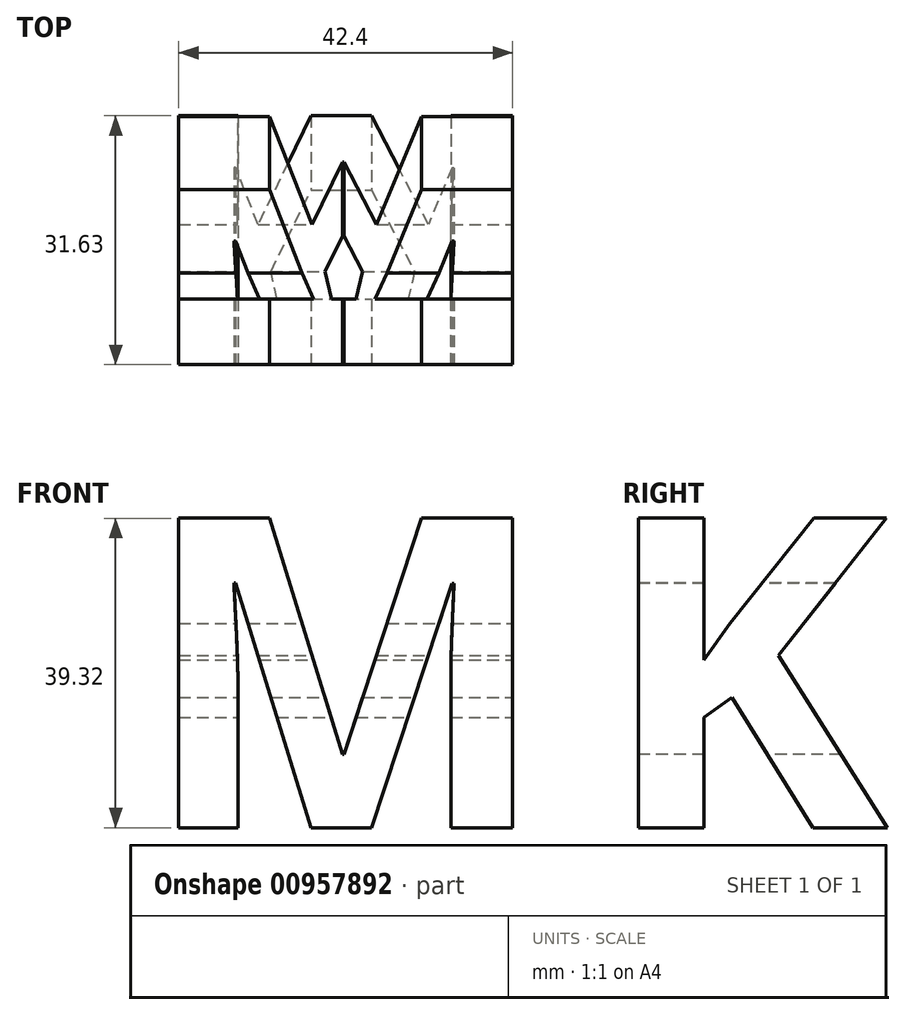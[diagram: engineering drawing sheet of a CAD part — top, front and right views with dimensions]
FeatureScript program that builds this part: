
annotation { "Feature Type Name" : "Feature", "Feature Type Description" : "" }
export const myFeature = defineFeature(function(context is Context, id is Id, definition is map)
    precondition{}
    {
        {
            var Q0;
            Q0=qCreatedBy(makeId("Front.planeOp"),FACE);
            var sketch = newSketch(context, id + "F0", { "sketchPlane" : qUnion([Q0])});
            skText(sketch, "E0", { "text": "M", "fontName": "OpenSans-Bold.ttf"});
            const initialGuessF0  = {"E0": [0, 0, 1, 0, 0.04]};
            skSetInitialGuess(sketch, initialGuessF0);
            skSolve(sketch);
        }
        {
            var Q0;
            Q0=makeQuery(id+"F0.imprint","IMPRINT",FACE,{"disambiguationData":[TD([[makeQuery(id+"F0.imprint","IMPRINT",EDGE,{"derivedFrom":sQuery(id+"F0.wireOp",EDGE,"E0.sketch_text.stroke-0")}),-1.0]])]});
            extrude(context, id + "F1", {"entities" : qUnion([Q0]), "flatOperationType" : FlatOperationType.REMOVE, "oppositeDirection" : true, "depth" : 40 * mm, "offsetDistance" : 25 * mm, "domain" : OperationDomain.MODEL});
        }
        {
            var Q0;
            Q0=makeQuery(id+"F1.opExtrude","SWEPT_FACE",FACE,{"disambiguationData":[OSD([sQuery(id+"F0.wireOp",EDGE,"E0.sketch_text.stroke-11")])]});
            var sketch = newSketch(context, id + "F2", { "sketchPlane" : qUnion([Q0])});
            skText(sketch, "E1", { "text": "K", "fontName": "OpenSans-Bold.ttf"});
            const initialGuessF2  = {"E1": [0, 0, 1, 0, 0.03966]};
            skSetInitialGuess(sketch, initialGuessF2);
            skSolve(sketch);
        }
        {
            var Q0;
            Q0 = qSketchRegion(id + "F2", true);
            var Q1;
            Q1=makeQuery(id+"F1.opExtrude","SWEPT_FACE",FACE,{"disambiguationData":[OSD([sQuery(id+"F0.wireOp",EDGE,"E0.sketch_text.stroke-5")])]});
            extrude(context, id + "F3", {"entities" : qUnion([Q0]), "endBound" : BoundingType.UP_TO_SURFACE, "oppositeDirection" : true, "depth" : 26.3 * mm, "endBoundEntityFace" : qUnion([Q1]), "offsetDistance" : 25 * mm});
        }
        {
            var Q0;
            Q0=makeQuery(id+"F3.opExtrude","SWEPT_BODY",BODY,{"disambiguationData":[OSD([sQuery(id+"F2.wireOp",EDGE,"E1.sketch_text.stroke-0"),sQuery(id+"F2.wireOp",EDGE,"E1.sketch_text.stroke-1"),sQuery(id+"F2.wireOp",EDGE,"E1.sketch_text.stroke-2"),sQuery(id+"F2.wireOp",EDGE,"E1.sketch_text.stroke-3"),sQuery(id+"F2.wireOp",EDGE,"E1.sketch_text.stroke-4"),sQuery(id+"F2.wireOp",EDGE,"E1.sketch_text.stroke-5"),sQuery(id+"F2.wireOp",EDGE,"E1.sketch_text.stroke-6"),sQuery(id+"F2.wireOp",EDGE,"E1.sketch_text.stroke-7"),sQuery(id+"F2.wireOp",EDGE,"E1.sketch_text.stroke-8"),sQuery(id+"F2.wireOp",EDGE,"E1.sketch_text.stroke-9"),sQuery(id+"F2.wireOp",EDGE,"E1.sketch_text.stroke-10"),sQuery(id+"F2.wireOp",EDGE,"E1.sketch_text.stroke-11"),sQuery(id+"F2.wireOp",EDGE,"E1.sketch_text.stroke-12")])]});
            var Q1;
            Q1=makeQuery(id+"F1.opExtrude","SWEPT_BODY",BODY,{"disambiguationData":[OSD([sQuery(id+"F0.wireOp",EDGE,"E0.sketch_text.stroke-0"),sQuery(id+"F0.wireOp",EDGE,"E0.sketch_text.stroke-1"),sQuery(id+"F0.wireOp",EDGE,"E0.sketch_text.stroke-2"),sQuery(id+"F0.wireOp",EDGE,"E0.sketch_text.stroke-3"),sQuery(id+"F0.wireOp",EDGE,"E0.sketch_text.stroke-4"),sQuery(id+"F0.wireOp",EDGE,"E0.sketch_text.stroke-5"),sQuery(id+"F0.wireOp",EDGE,"E0.sketch_text.stroke-6"),sQuery(id+"F0.wireOp",EDGE,"E0.sketch_text.stroke-7"),sQuery(id+"F0.wireOp",EDGE,"E0.sketch_text.stroke-8"),sQuery(id+"F0.wireOp",EDGE,"E0.sketch_text.stroke-9"),sQuery(id+"F0.wireOp",EDGE,"E0.sketch_text.stroke-10"),sQuery(id+"F0.wireOp",EDGE,"E0.sketch_text.stroke-11"),sQuery(id+"F0.wireOp",EDGE,"E0.sketch_text.stroke-12"),sQuery(id+"F0.wireOp",EDGE,"E0.sketch_text.stroke-13"),sQuery(id+"F0.wireOp",EDGE,"E0.sketch_text.stroke-14"),sQuery(id+"F0.wireOp",EDGE,"E0.sketch_text.stroke-15"),sQuery(id+"F0.wireOp",EDGE,"E0.sketch_text.stroke-16"),sQuery(id+"F0.wireOp",EDGE,"E0.sketch_text.stroke-17"),sQuery(id+"F0.wireOp",EDGE,"E0.sketch_text.stroke-18")])]});
            var Q2;
            Q2=makeQuery(id+"F1.opExtrude","SWEPT_BODY",BODY,{"disambiguationData":[OSD([sQuery(id+"F0.wireOp",EDGE,"E0.sketch_text.stroke-0"),sQuery(id+"F0.wireOp",EDGE,"E0.sketch_text.stroke-1"),sQuery(id+"F0.wireOp",EDGE,"E0.sketch_text.stroke-2"),sQuery(id+"F0.wireOp",EDGE,"E0.sketch_text.stroke-3"),sQuery(id+"F0.wireOp",EDGE,"E0.sketch_text.stroke-4"),sQuery(id+"F0.wireOp",EDGE,"E0.sketch_text.stroke-5"),sQuery(id+"F0.wireOp",EDGE,"E0.sketch_text.stroke-6"),sQuery(id+"F0.wireOp",EDGE,"E0.sketch_text.stroke-7"),sQuery(id+"F0.wireOp",EDGE,"E0.sketch_text.stroke-8"),sQuery(id+"F0.wireOp",EDGE,"E0.sketch_text.stroke-9"),sQuery(id+"F0.wireOp",EDGE,"E0.sketch_text.stroke-10"),sQuery(id+"F0.wireOp",EDGE,"E0.sketch_text.stroke-11"),sQuery(id+"F0.wireOp",EDGE,"E0.sketch_text.stroke-12"),sQuery(id+"F0.wireOp",EDGE,"E0.sketch_text.stroke-13"),sQuery(id+"F0.wireOp",EDGE,"E0.sketch_text.stroke-14"),sQuery(id+"F0.wireOp",EDGE,"E0.sketch_text.stroke-15"),sQuery(id+"F0.wireOp",EDGE,"E0.sketch_text.stroke-16"),sQuery(id+"F0.wireOp",EDGE,"E0.sketch_text.stroke-17"),sQuery(id+"F0.wireOp",EDGE,"E0.sketch_text.stroke-18")])]});
            booleanBodies(context, id + "F4", {"operationType" : BooleanOperationType.INTERSECTION, "tools" : qUnion([Q0, Q1]), "targets" : qUnion([Q2])});
        }
        {
            var Q0;
            Q0=makeQuery(id+"F4.opBoolean","INTERSECT",BODY,{"derivedFrom":[makeQuery(id+"F1.opExtrude","SWEPT_BODY",BODY,{"disambiguationData":[OSD([sQuery(id+"F0.wireOp",EDGE,"E0.sketch_text.stroke-0"),sQuery(id+"F0.wireOp",EDGE,"E0.sketch_text.stroke-1"),sQuery(id+"F0.wireOp",EDGE,"E0.sketch_text.stroke-2"),sQuery(id+"F0.wireOp",EDGE,"E0.sketch_text.stroke-3"),sQuery(id+"F0.wireOp",EDGE,"E0.sketch_text.stroke-4"),sQuery(id+"F0.wireOp",EDGE,"E0.sketch_text.stroke-5"),sQuery(id+"F0.wireOp",EDGE,"E0.sketch_text.stroke-6"),sQuery(id+"F0.wireOp",EDGE,"E0.sketch_text.stroke-7"),sQuery(id+"F0.wireOp",EDGE,"E0.sketch_text.stroke-8"),sQuery(id+"F0.wireOp",EDGE,"E0.sketch_text.stroke-9"),sQuery(id+"F0.wireOp",EDGE,"E0.sketch_text.stroke-10"),sQuery(id+"F0.wireOp",EDGE,"E0.sketch_text.stroke-11"),sQuery(id+"F0.wireOp",EDGE,"E0.sketch_text.stroke-12"),sQuery(id+"F0.wireOp",EDGE,"E0.sketch_text.stroke-13"),sQuery(id+"F0.wireOp",EDGE,"E0.sketch_text.stroke-14"),sQuery(id+"F0.wireOp",EDGE,"E0.sketch_text.stroke-15"),sQuery(id+"F0.wireOp",EDGE,"E0.sketch_text.stroke-16"),sQuery(id+"F0.wireOp",EDGE,"E0.sketch_text.stroke-17"),sQuery(id+"F0.wireOp",EDGE,"E0.sketch_text.stroke-18")])]}),makeQuery(id+"F3.opExtrude","SWEPT_BODY",BODY,{"disambiguationData":[OSD([sQuery(id+"F2.wireOp",EDGE,"E1.sketch_text.stroke-0"),sQuery(id+"F2.wireOp",EDGE,"E1.sketch_text.stroke-1"),sQuery(id+"F2.wireOp",EDGE,"E1.sketch_text.stroke-2"),sQuery(id+"F2.wireOp",EDGE,"E1.sketch_text.stroke-3"),sQuery(id+"F2.wireOp",EDGE,"E1.sketch_text.stroke-4"),sQuery(id+"F2.wireOp",EDGE,"E1.sketch_text.stroke-5"),sQuery(id+"F2.wireOp",EDGE,"E1.sketch_text.stroke-6"),sQuery(id+"F2.wireOp",EDGE,"E1.sketch_text.stroke-7"),sQuery(id+"F2.wireOp",EDGE,"E1.sketch_text.stroke-8"),sQuery(id+"F2.wireOp",EDGE,"E1.sketch_text.stroke-9"),sQuery(id+"F2.wireOp",EDGE,"E1.sketch_text.stroke-10"),sQuery(id+"F2.wireOp",EDGE,"E1.sketch_text.stroke-11"),sQuery(id+"F2.wireOp",EDGE,"E1.sketch_text.stroke-12")])]})]});
            var Q1;
            Q1=makeQuery(id+"F3.opExtrude","CAP_VERTEX",VERTEX,{"disambiguationData":[OSD([sQuery(id+"F0.wireOp",EDGE,"E0.sketch_text.stroke-11"),sQuery(id+"F0.wireOp",EDGE,"E0.sketch_text.stroke-12"),sQuery(id+"F2.wireOp",EDGE,"E1.sketch_text.stroke-0"),sQuery(id+"F2.wireOp",EDGE,"E1.sketch_text.stroke-12")])],"isStart":true});
            transform(context, id + "F5", {"entities" : qUnion([Q0]), "transformType" : TransformType.SCALE_UNIFORMLY, "scale" : 1, "scalePoint" : qUnion([Q1]), "makeCopy" : false});
        }
    });
